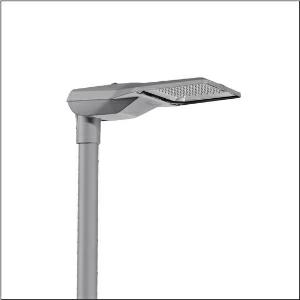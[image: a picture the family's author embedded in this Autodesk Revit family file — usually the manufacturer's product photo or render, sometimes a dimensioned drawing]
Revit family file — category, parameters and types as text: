
# Revit family: streetlight_sl_21_midi___st1_0a_5xe3d43s08nb_04c9
name_source: partatom
category: Lighting Fixtures
units: mm (PartAtom-declared; Revit-internal decimal feet)

## family parameters
Cut with Voids When Loaded = No
Host = Face
Light Source = No
Part Type = Normal
Room Calculation Point = No
Round Connector Dimension = Use Diameter
Shared = No

## types (1)
- --- (1 x LED, 23710 lm, 151.2 W, 4000K)
    Apparent Load = 151 VA
    CIE Flux Codes = 40 73 97 100 100
    Color Rendering = 70
    Color Temperature = 4000K
    Default Elevation = 1800 mm
    Description = Streetlight SL 21 midi, mast luminaire, primary light control with lens, of PMMA, primary optical cover: cover, of toughened safety glass, transparent, light distribution: ST1.0a, light emission: direct distribution, primary light characteristic: asymmetric, installation type: side-entry, post-top, LED, High Power LED, rated luminous flux: 23.710lm, luminous efficacy: 157lm/W, light colour: 740, colour temperature: 4000K, control: overheat protection, constant luminous flux control, time-dependent luminous flux control, flexible luminous flux parameterisation, presetting dimming logarithmic, mains connection: 230..240V, AC, 50/60Hz, start of lifetime: 151W, end of service life: 157W, reduction: 70W, luminaire housing, of diecast aluminium, powder-coated, Siteco® metallic grey (DB 702S), corrosivity category C5 mid according to DIN EN ISO 12944, please order mast flange separately, inclination adjustable: 0°, 5°, 10°, 15°, sealing non-destructively replaceable, multi-level sealing system, length: 644mm, width: 335mm, height: 110mm, mast flange for spigot size: 42mm (side-entry): 5XC10008XM4, 60/48mm (side-entry/post-top): 5XC10108XM2, 76/60mm (side-entry/post-top): 5XC10108XM1, Smart Interface above, protection rating (complete): IP66, insulation class (complete): insulation class II (safety insulation), certification: CE, ENEC, ENEC+, VDE, impact resistance: IK09, permissible operating ambient temperature for outdoor applications: -40..+50°C, standard-compliant lighting for roads and squares, packaging unit: 1 piece

Light Distribution: ST1.0a
    Height = 111 mm
    Lamp = 1 x LED
    Lamp Light Flux = 23710 lm
    Lamp Power = 151.2 W
    Lamp count = 1
    Length = 644 mm
    Luminous efficacy = 157 lm/W
    Manufacturer = Siteco
    ModVariant = No
    Model = 5XE3D43S08NB
    Number of Poles = 1
    OnlyDefault = Yes
    Power Factor = 1
    Product Name = Streetlight SL 21 midi | ST1.0a
    Product group = mast luminaire | pylon top
    ProductGroupID = 6100
    Protection Class = Protection class II
    Protection Degree = IP 66
    RLX_Detail_Level = 1
    RLX_Emergency_Light_Flux = 0 lm
    RLX_Emergency_Type = 0
    RLX_Emergency_Type_DB = No
    RlxData = <blob elided: 90849 chars, md5=2709b9af>
    Socket = socket
    Standby Power = 0 W
    System Light Flux = 23710 lm
    System Power = 151 W
    Type Comments = factory setting: luminous flux: 100 % | dim-lin: 254 | 802 mA
    Type Image = l_1004302.jpg
    URL = http://relux.com
    VarID = @adj_121161
    Voltage = 0 V
    Weight = 0.00 kg
    Width = 336 mm

## geometry (parser evidence)
native form markers: Blend x4, Sweep x12
no freeform markers — native parametric forms only
